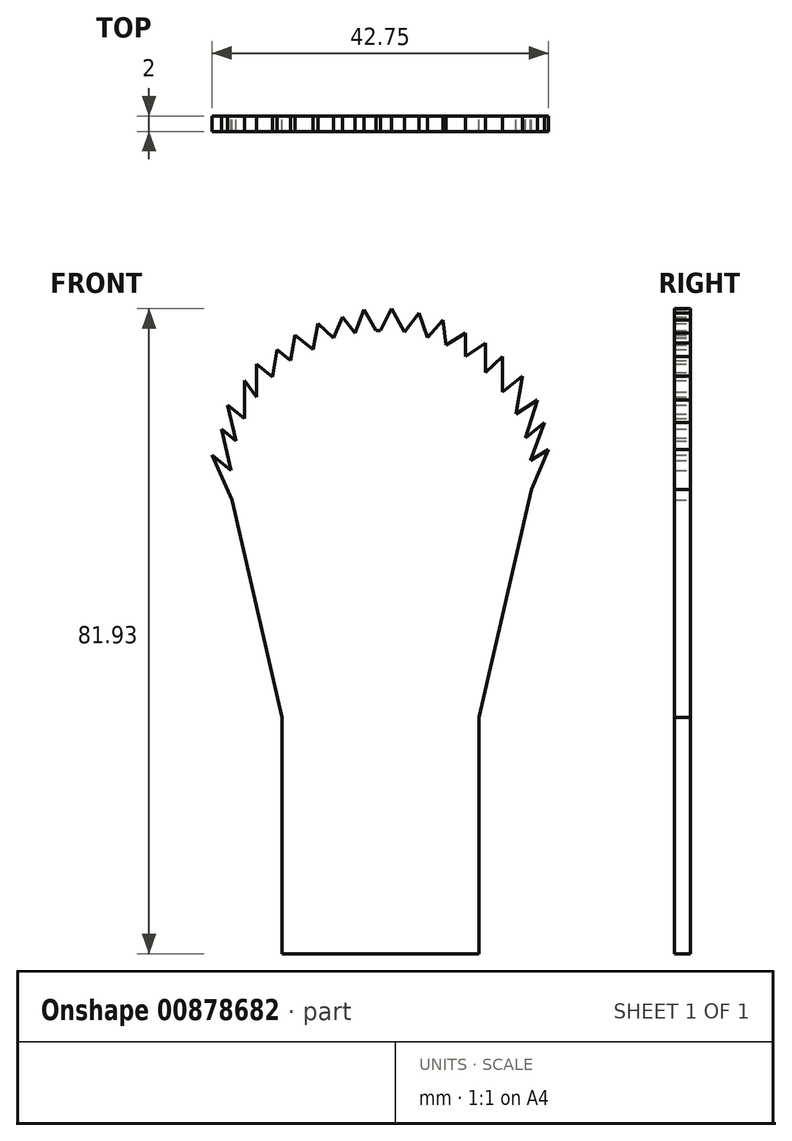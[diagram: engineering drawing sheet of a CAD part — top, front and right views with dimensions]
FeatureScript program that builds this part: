
annotation { "Feature Type Name" : "Feature", "Feature Type Description" : "" }
export const myFeature = defineFeature(function(context is Context, id is Id, definition is map)
    precondition{}
    {
        {
            var Q0;
            Q0=qCreatedBy(makeId("Front.planeOp"),FACE);
            var sketch = newSketch(context, id + "F0", { "sketchPlane" : qUnion([Q0])});
            skLineSegment(sketch, "E0.top", {"start": v(12.5, -15) * mm, "end": v(-12.5, -15) * mm});
            skLineSegment(sketch, "E0.left", {"start": v(12.5, 15) * mm, "end": v(12.5, -15) * mm});
            skLineSegment(sketch, "E0.right", {"start": v(-12.5, 15) * mm, "end": v(-12.5, -15) * mm});
            skPoint(sketch, "E0.middle", {"position": v(0, 0) * mm});
            skLineSegment(sketch, "E1", {"start": v(-12.5, 15) * mm, "end": v(-18.88, 42.65) * mm});
            skLineSegment(sketch, "E2", {"start": v(12.5, 15) * mm, "end": v(19.19, 43.97) * mm});
            skLineSegment(sketch, "E3", {"start": v(-18.88, 42.65) * mm, "end": v(-21.4, 48.38) * mm});
            skLineSegment(sketch, "E4", {"start": v(-21.4, 48.38) * mm, "end": v(-18.99, 46.38) * mm});
            skLineSegment(sketch, "E5", {"start": v(-18.99, 46.38) * mm, "end": v(-20.2, 51.63) * mm});
            skPoint(sketch, "E5.endSnap0", {"position": v(-20.2, 47.38) * mm});
            skLineSegment(sketch, "E6", {"start": v(-20.2, 51.63) * mm, "end": v(-18.35, 50.11) * mm});
            skLineSegment(sketch, "E7", {"start": v(-18.35, 50.11) * mm, "end": v(-19.41, 54.72) * mm});
            skLineSegment(sketch, "E8", {"start": v(-19.41, 54.72) * mm, "end": v(-17.3, 52.99) * mm});
            skLineSegment(sketch, "E9", {"start": v(-17.3, 52.99) * mm, "end": v(-17.3, 57.8) * mm});
            skLineSegment(sketch, "E10", {"start": v(-17.3, 57.8) * mm, "end": v(-15.77, 55.73) * mm});
            skLineSegment(sketch, "E11", {"start": v(-15.77, 55.73) * mm, "end": v(-15.77, 59.92) * mm});
            skLineSegment(sketch, "E12", {"start": v(-15.77, 59.92) * mm, "end": v(-13.73, 58.25) * mm});
            skLineSegment(sketch, "E13", {"start": v(-13.73, 58.25) * mm, "end": v(-13.18, 61.77) * mm});
            skLineSegment(sketch, "E14", {"start": v(-13.18, 61.77) * mm, "end": v(-11.41, 60.32) * mm});
            skLineSegment(sketch, "E15", {"start": v(-11.41, 60.32) * mm, "end": v(-10.84, 63.6) * mm});
            skLineSegment(sketch, "E16", {"start": v(-10.84, 63.6) * mm, "end": v(-8.6, 61.77) * mm});
            skLineSegment(sketch, "E17", {"start": v(-8.6, 61.77) * mm, "end": v(-7.93, 65.02) * mm});
            skLineSegment(sketch, "E18", {"start": v(-7.93, 65.02) * mm, "end": v(-5.95, 63.18) * mm});
            skLineSegment(sketch, "E19", {"start": v(-5.95, 63.18) * mm, "end": v(-4.82, 65.87) * mm});
            skLineSegment(sketch, "E20", {"start": v(-4.82, 65.87) * mm, "end": v(-3.23, 63.87) * mm});
            skLineSegment(sketch, "E21", {"start": v(-3.23, 63.87) * mm, "end": v(-2.13, 66.8) * mm});
            skLineSegment(sketch, "E22", {"start": v(-2.13, 66.8) * mm, "end": v(-0.57, 64.15) * mm});
            skLineSegment(sketch, "E23", {"start": v(0, 64.16) * mm, "end": v(1.42, 66.93) * mm});
            skLineSegment(sketch, "E24", {"start": v(1.42, 66.93) * mm, "end": v(3.03, 63.94) * mm});
            skLineSegment(sketch, "E25", {"start": v(3.03, 63.94) * mm, "end": v(4.9, 66.37) * mm});
            skLineSegment(sketch, "E26", {"start": v(4.9, 66.37) * mm, "end": v(5.95, 63.24) * mm});
            skLineSegment(sketch, "E27", {"start": v(5.95, 63.24) * mm, "end": v(7.94, 65.48) * mm});
            skLineSegment(sketch, "E28", {"start": v(7.94, 65.48) * mm, "end": v(8.3, 62.31) * mm});
            skLineSegment(sketch, "E29", {"start": v(8.3, 62.31) * mm, "end": v(10.8, 63.87) * mm});
            skLineSegment(sketch, "E30", {"start": v(10.8, 63.87) * mm, "end": v(10.8, 60.89) * mm});
            skLineSegment(sketch, "E31", {"start": v(10.8, 60.89) * mm, "end": v(13.36, 62.56) * mm});
            skLineSegment(sketch, "E32", {"start": v(13.36, 62.56) * mm, "end": v(13.36, 58.82) * mm});
            skLineSegment(sketch, "E33", {"start": v(13.36, 58.82) * mm, "end": v(15.5, 60.89) * mm});
            skLineSegment(sketch, "E34", {"start": v(15.5, 60.89) * mm, "end": v(15.5, 56.37) * mm});
            skLineSegment(sketch, "E35", {"start": v(15.5, 56.37) * mm, "end": v(18, 58.4) * mm});
            skLineSegment(sketch, "E36", {"start": v(18, 58.4) * mm, "end": v(17.23, 53.54) * mm});
            skLineSegment(sketch, "E37", {"start": v(17.23, 53.54) * mm, "end": v(19.9, 55.36) * mm});
            skLineSegment(sketch, "E38", {"start": v(19.9, 55.36) * mm, "end": v(18.42, 50.49) * mm});
            skLineSegment(sketch, "E39", {"start": v(18.42, 50.49) * mm, "end": v(20.8, 52.5) * mm});
            skLineSegment(sketch, "E40", {"start": v(20.8, 52.5) * mm, "end": v(19.04, 47.65) * mm});
            skLineSegment(sketch, "E41", {"start": v(19.04, 47.65) * mm, "end": v(21.34, 49.04) * mm});
            skLineSegment(sketch, "E42", {"start": v(21.34, 49.04) * mm, "end": v(19.19, 43.97) * mm});
            skArc(sketch, "E43.trimOffspring", {"start": v(-8.53, 62.1) * mm, "mid": v(-8.68, 62.03) * mm, "end": v(-8.83, 61.95) * mm});
            skArc(sketch, "E44.trimOffspring", {"start": v(0, 64.16) * mm, "mid": v(-0.28, 64.16) * mm, "end": v(-0.57, 64.15) * mm});
            skSolve(sketch);
        }
        {
            var Q0;
            Q0=makeQuery(id+"F0.imprint","IMPRINT",FACE,{"disambiguationData":[TD([[makeQuery(id+"F0.imprint","IMPRINT",EDGE,{"derivedFrom":sQuery(id+"F0.wireOp",EDGE,"E0.top")}),-1.0]])]});
            extrude(context, id + "F1", {"entities" : qUnion([Q0]), "depth" : 2 * mm, "offsetDistance" : 25 * mm});
        }
    });
